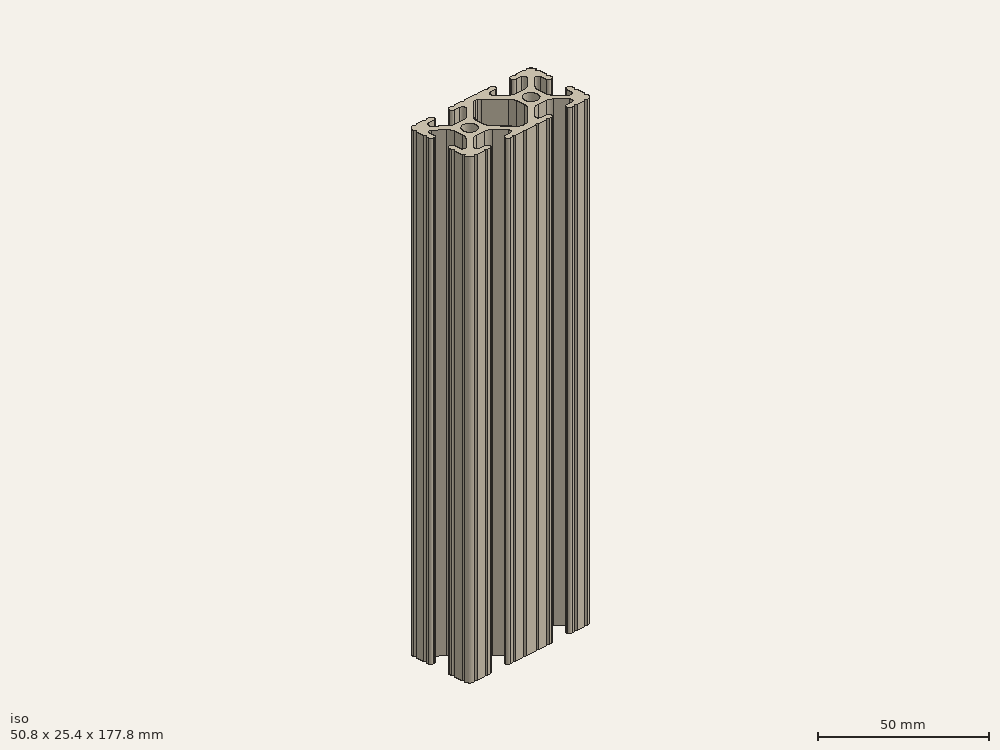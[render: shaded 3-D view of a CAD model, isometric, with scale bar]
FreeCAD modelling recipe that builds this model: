
FCSTD DOCUMENT  (FreeCAD 0.19R24267 (Git))
Label: 1020-7
License: All rights reserved
LicenseURL: http://en.wikipedia.org/wiki/All_rights_reserved
objects: Sketcher::SketchObject×1, Part::Extrusion×1
note: 2 computed .brp shape members not serialized (recipe doc carries the construction recipe); baked Part::Feature solids carry a one-line shape summary decoded from their .brp

FEATURE [Sketcher::SketchObject] Sketch162
  FullyConstrained = false
  sketch-geometry (162):
    g0: LineSegment StartX=7.25951 StartY=3.86941 StartZ=0 EndX=1.54575 EndY=9.57277 EndZ=0
    g1: LineSegment StartX=8.41248 StartY=-10.4902 StartZ=0 EndX=6.28364 EndY=-10.4902 EndZ=0
    g2: ArcOfCircle CenterX=8.41255 CenterY=-11.651 CenterZ=0 NormalX=0 NormalY=0 NormalZ=1 AngleXU=0 Radius=1.04895 StartAngle=4.71239 EndAngle=6.28319
    g3: LineSegment StartX=5.53258 StartY=-8.66607 StartZ=0 EndX=8.80999 EndY=-5.41626 EndZ=0
    g4: LineSegment StartX=9.4615 StartY=-11.651 StartZ=0 EndX=9.4615 EndY=-11.5392 EndZ=0
    g5: ArcOfCircle CenterX=8.41248 CenterY=-11.5392 CenterZ=0 NormalX=0 NormalY=0 NormalZ=1 AngleXU=0 Radius=1.04902 StartAngle=1.15714e-07 EndAngle=1.5708
    g6: ArcOfCircle CenterX=6.28364 CenterY=-9.42351 CenterZ=0 NormalX=0 NormalY=0 NormalZ=1 AngleXU=0 Radius=1.06669 StartAngle=2.35197 EndAngle=4.71239
    g7: LineSegment StartX=-7.28286 StartY=-3.84586 StartZ=0 EndX=-1.67557 EndY=-9.56109 EndZ=0
    g8: LineSegment StartX=1.50403 StartY=-9.57645 StartZ=0 EndX=7.25205 EndY=-3.87684 EndZ=0
    g9: LineSegment StartX=-0.551457 StartY=-10.033 StartZ=0 EndX=0.3952 EndY=-10.033 EndZ=0
    g10: LineSegment StartX=-1.54575 StartY=9.57277 StartZ=0 EndX=-7.25951 EndY=3.86941 EndZ=0
    g11: ArcOfCircle CenterX=0.3952 CenterY=-8.4582 CenterZ=0 NormalX=0 NormalY=0 NormalZ=1 AngleXU=0 Radius=1.5748 StartAngle=4.71239 EndAngle=5.49356
    g12: ArcOfCircle CenterX=5.0165 CenterY=-1.6223 CenterZ=0 NormalX=0 NormalY=0 NormalZ=1 AngleXU=0 Radius=3.175 StartAngle=5.49356 EndAngle=6.28319
    g13: LineSegment StartX=8.1915 StartY=-1.6223 StartZ=0 EndX=8.1915 EndY=1.6223 EndZ=0
    g14: LineSegment StartX=0.433213 StartY=10.033 StartZ=0 EndX=-0.433213 EndY=10.033 EndZ=0
    g15: ArcOfCircle CenterX=-0.551456 CenterY=-8.4582 CenterZ=0 NormalX=0 NormalY=0 NormalZ=1 AngleXU=0 Radius=1.5748 StartAngle=3.91746 EndAngle=4.71239
    g16: ArcOfCircle CenterX=-5.0165 CenterY=1.6223 CenterZ=0 NormalX=0 NormalY=0 NormalZ=1 AngleXU=0 Radius=3.175 StartAngle=2.35528 EndAngle=3.14159
    g17: ArcOfCircle CenterX=-0.433213 CenterY=8.4582 CenterZ=0 NormalX=0 NormalY=0 NormalZ=1 AngleXU=0 Radius=1.5748 StartAngle=1.5708 EndAngle=2.35528
    g18: ArcOfCircle CenterX=5.0165 CenterY=1.6223 CenterZ=0 NormalX=0 NormalY=0 NormalZ=1 AngleXU=0 Radius=3.175 StartAngle=2.15656e-07 EndAngle=0.78631
    g19: Circle CenterX=12.7 CenterY=-2.5e-15 CenterZ=0 NormalX=0 NormalY=0 NormalZ=-1 AngleXU=0 Radius=2.6035
    g20: Circle CenterX=-12.7 CenterY=2.5e-15 CenterZ=0 NormalX=0 NormalY=0 NormalZ=-1 AngleXU=0 Radius=2.6035
    g21: LineSegment StartX=-8.1915 StartY=1.6223 StartZ=0 EndX=-8.1915 EndY=-1.6223 EndZ=0
    g22: LineSegment StartX=-2.13358 StartY=-12.7 StartZ=0 EndX=2.13358 EndY=-12.7 EndZ=0
    g23: ArcOfCircle CenterX=-5.0165 CenterY=-1.6223 CenterZ=0 NormalX=0 NormalY=0 NormalZ=1 AngleXU=0 Radius=3.175 StartAngle=3.14159 EndAngle=3.91746
    g24: LineSegment StartX=3.14958 StartY=-12.7 StartZ=0 EndX=6.3669 EndY=-12.7 EndZ=0
    g25: ArcOfCircle CenterX=6.8749 CenterY=-12.7 CenterZ=0 NormalX=0 NormalY=0 NormalZ=1 AngleXU=0 Radius=0.508 StartAngle=0 EndAngle=3.14159
    g26: LineSegment StartX=-6.28939 StartY=-10.4902 StartZ=0 EndX=-8.41248 EndY=-10.4902 EndZ=0
    g27: LineSegment StartX=-8.41255 StartY=-12.7 StartZ=0 EndX=-7.38288 EndY=-12.7 EndZ=0
    g28: ArcOfCircle CenterX=0.433213 CenterY=8.4582 CenterZ=0 NormalX=0 NormalY=0 NormalZ=1 AngleXU=0 Radius=1.5748 StartAngle=0.78631 EndAngle=1.5708
    g29: ArcOfCircle CenterX=2.64158 CenterY=-12.7 CenterZ=0 NormalX=0 NormalY=0 NormalZ=1 AngleXU=0 Radius=0.508 StartAngle=0 EndAngle=3.14159
    g30: ArcOfCircle CenterX=-16.9875 CenterY=-11.5392 CenterZ=0 NormalX=0 NormalY=0 NormalZ=1 AngleXU=0 Radius=1.04902 StartAngle=1.16223e-07 EndAngle=1.5708
    g31: LineSegment StartX=-8.81696 StartY=-5.44724 StartZ=0 EndX=-5.56415 EndY=-8.76265 EndZ=0
    g32: LineSegment StartX=-16.9875 StartY=-10.4902 StartZ=0 EndX=-19.1164 EndY=-10.4902 EndZ=0
    g33: ArcOfCircle CenterX=-11.0833 CenterY=-7.6708 CenterZ=0 NormalX=0 NormalY=0 NormalZ=1 AngleXU=0 Radius=3.175 StartAngle=0.775866 EndAngle=1.5708
    g34: ArcOfCircle CenterX=-14.3449 CenterY=-7.6708 CenterZ=0 NormalX=0 NormalY=0 NormalZ=1 AngleXU=0 Radius=3.175 StartAngle=1.5708 EndAngle=2.3692
    g35: ArcOfCircle CenterX=-19.1164 CenterY=-9.4742 CenterZ=0 NormalX=0 NormalY=0 NormalZ=1 AngleXU=0 Radius=1.016 StartAngle=2.3692 EndAngle=4.71239
    g36: ArcOfCircle CenterX=-8.41248 CenterY=-11.5392 CenterZ=0 NormalX=0 NormalY=0 NormalZ=1 AngleXU=0 Radius=1.04902 StartAngle=1.5708 EndAngle=3.14159
    g37: LineSegment StartX=7.3829 StartY=-12.7 StartZ=0 EndX=8.41255 EndY=-12.7 EndZ=0
    g38: ArcOfCircle CenterX=-8.41255 CenterY=-11.651 CenterZ=0 NormalX=0 NormalY=0 NormalZ=1 AngleXU=0 Radius=1.04895 StartAngle=3.14159 EndAngle=4.71239
    g39: ArcOfCircle CenterX=14.3545 CenterY=-7.6708 CenterZ=0 NormalX=0 NormalY=0 NormalZ=1 AngleXU=0 Radius=3.175 StartAngle=0.789627 EndAngle=1.5708
    g40: ArcOfCircle CenterX=20.3835 CenterY=-1.55362 CenterZ=0 NormalX=0 NormalY=0 NormalZ=1 AngleXU=0 Radius=3.175 StartAngle=3.14159 EndAngle=3.93122
    g41: LineSegment StartX=23.1902 StartY=6.498 StartZ=0 EndX=23.1902 EndY=4.28752 EndZ=0
    g42: LineSegment StartX=-14.3449 StartY=-4.4958 StartZ=0 EndX=-11.0833 EndY=-4.4958 EndZ=0
    g43: LineSegment StartX=-19.8441 StartY=-8.76517 StartZ=0 EndX=-16.619 EndY=-5.45511 EndZ=0
    g44: LineSegment StartX=-6.36688 StartY=-12.7 StartZ=0 EndX=-3.14958 EndY=-12.7 EndZ=0
    g45: ArcOfCircle CenterX=-6.28939 CenterY=-9.4742 CenterZ=0 NormalX=0 NormalY=0 NormalZ=1 AngleXU=0 Radius=1.016 StartAngle=4.71239 EndAngle=7.05905
    g46: LineSegment StartX=-9.4615 StartY=-11.5392 StartZ=0 EndX=-9.4615 EndY=-11.6511 EndZ=0
    g47: ArcOfCircle CenterX=-6.87488 CenterY=-12.7 CenterZ=0 NormalX=0 NormalY=0 NormalZ=1 AngleXU=0 Radius=0.508 StartAngle=0 EndAngle=3.14159
    g48: LineSegment StartX=-15.9385 StartY=-11.651 StartZ=0 EndX=-15.9385 EndY=-11.5392 EndZ=0
    g49: ArcOfCircle CenterX=-2.64158 CenterY=-12.7 CenterZ=0 NormalX=0 NormalY=0 NormalZ=1 AngleXU=0 Radius=0.508 StartAngle=0 EndAngle=3.14159
    g50: ArcOfCircle CenterX=22.1596 CenterY=-6.33474 CenterZ=0 NormalX=0 NormalY=0 NormalZ=1 AngleXU=0 Radius=1.03057 StartAngle=3.93122 EndAngle=6.28319
    g51: ArcOfCircle CenterX=25.4 CenterY=5.82513 CenterZ=0 NormalX=0 NormalY=0 NormalZ=1 AngleXU=0 Radius=0.508 StartAngle=1.5708 EndAngle=4.71239
    g52: LineSegment StartX=25.4 StartY=6.33313 StartZ=0 EndX=25.4 EndY=9.5504 EndZ=0
    g53: LineSegment StartX=19.0331 StartY=-12.7 StartZ=0 EndX=22.2504 EndY=-12.7 EndZ=0
    g54: ArcOfCircle CenterX=20.3835 CenterY=1.69518 CenterZ=0 NormalX=0 NormalY=0 NormalZ=1 AngleXU=0 Radius=3.175 StartAngle=2.35528 EndAngle=3.14159
    g55: LineSegment StartX=16.9875 StartY=-12.7 StartZ=0 EndX=18.0171 EndY=-12.7 EndZ=0
    g56: ArcOfCircle CenterX=23.2918 CenterY=10.5918 CenterZ=0 NormalX=0 NormalY=0 NormalZ=1 AngleXU=0 Radius=2.1082 StartAngle=6.27114 EndAngle=7.86603
    g57: ArcOfCircle CenterX=24.2392 CenterY=-4.28752 CenterZ=0 NormalX=0 NormalY=0 NormalZ=1 AngleXU=0 Radius=1.04902 StartAngle=1.5708 EndAngle=3.14159
    g58: ArcOfCircle CenterX=24.401 CenterY=-4.23752 CenterZ=0 NormalX=0 NormalY=0 NormalZ=1 AngleXU=0 Radius=0.99902 StartAngle=1.41033e-07 EndAngle=1.5708
    g59: LineSegment StartX=16.59 StartY=-5.41626 StartZ=0 EndX=19.8674 EndY=-8.66607 EndZ=0
    g60: ArcOfCircle CenterX=16.9875 CenterY=-11.5392 CenterZ=0 NormalX=0 NormalY=0 NormalZ=1 AngleXU=0 Radius=1.04902 StartAngle=1.5708 EndAngle=3.14159
    g61: LineSegment StartX=22.2504 StartY=12.7 StartZ=0 EndX=19.0331 EndY=12.7 EndZ=0
    g62: ArcOfCircle CenterX=23.2918 CenterY=-10.5918 CenterZ=0 NormalX=0 NormalY=0 NormalZ=1 AngleXU=0 Radius=2.1082 StartAngle=4.70034 EndAngle=6.29523
    g63: ArcOfCircle CenterX=11.0455 CenterY=-7.6708 CenterZ=0 NormalX=0 NormalY=0 NormalZ=1 AngleXU=0 Radius=3.175 StartAngle=1.5708 EndAngle=2.35197
    g64: ArcOfCircle CenterX=22.7584 CenterY=12.7 CenterZ=0 NormalX=0 NormalY=0 NormalZ=1 AngleXU=0 Radius=0.508 StartAngle=3.14159 EndAngle=6.28288
    g65: LineSegment StartX=19.1164 StartY=-10.4902 StartZ=0 EndX=16.9875 EndY=-10.4902 EndZ=0
    g66: ArcOfCircle CenterX=22.7584 CenterY=-12.7 CenterZ=0 NormalX=0 NormalY=0 NormalZ=1 AngleXU=0 Radius=0.508 StartAngle=0.000301216 EndAngle=3.14159
    g67: ArcOfCircle CenterX=16.9875 CenterY=11.651 CenterZ=0 NormalX=0 NormalY=0 NormalZ=1 AngleXU=0 Radius=1.04902 StartAngle=1.5708 EndAngle=3.14159
    g68: ArcOfCircle CenterX=24.351 CenterY=4.28752 CenterZ=0 NormalX=0 NormalY=0 NormalZ=1 AngleXU=0 Radius=1.04902 StartAngle=4.71239 EndAngle=6.28319
    g69: ArcOfCircle CenterX=19.1164 CenterY=9.4742 CenterZ=0 NormalX=0 NormalY=0 NormalZ=1 AngleXU=0 Radius=1.016 StartAngle=5.49688 EndAngle=7.85398
    g70: LineSegment StartX=19.8341 StartY=8.75512 StartZ=0 EndX=16.4966 EndY=5.42369 EndZ=0
    g71: LineSegment StartX=18.0171 StartY=12.7 StartZ=0 EndX=16.9875 EndY=12.7 EndZ=0
    g72: ArcOfCircle CenterX=18.5251 CenterY=-12.7 CenterZ=0 NormalX=0 NormalY=0 NormalZ=1 AngleXU=0 Radius=0.508 StartAngle=0 EndAngle=3.14159
    g73: LineSegment StartX=15.9384 StartY=11.651 StartZ=0 EndX=15.9384 EndY=11.5392 EndZ=0
    g74: LineSegment StartX=16.9875 StartY=10.4902 StartZ=0 EndX=19.1164 EndY=10.4902 EndZ=0
    g75: LineSegment StartX=11.0455 StartY=-4.4958 StartZ=0 EndX=14.3545 EndY=-4.4958 EndZ=0
    g76: ArcOfCircle CenterX=14.2536 CenterY=7.6708 CenterZ=0 NormalX=0 NormalY=0 NormalZ=1 AngleXU=0 Radius=3.175 StartAngle=4.71239 EndAngle=5.49688
    g77: ArcOfCircle CenterX=25.4 CenterY=-5.82508 CenterZ=0 NormalX=0 NormalY=0 NormalZ=1 AngleXU=0 Radius=0.508 StartAngle=1.5708 EndAngle=4.71239
    g78: LineSegment StartX=18.1405 StartY=3.94229 StartZ=0 EndX=21.4316 EndY=7.22739 EndZ=0
    g79: LineSegment StartX=25.4 StartY=-5.31708 StartZ=0 EndX=25.4 EndY=-4.23752 EndZ=0
    g80: LineSegment StartX=14.2536 StartY=4.4958 StartZ=0 EndX=11.1464 EndY=4.4958 EndZ=0
    g81: ArcOfCircle CenterX=18.5251 CenterY=12.7 CenterZ=0 NormalX=0 NormalY=0 NormalZ=1 AngleXU=0 Radius=0.508 StartAngle=3.14159 EndAngle=6.28319
    g82: LineSegment StartX=23.1902 StartY=-4.28752 StartZ=0 EndX=23.1902 EndY=-6.33474 EndZ=0
    g83: LineSegment StartX=24.401 StartY=-3.2385 StartZ=0 EndX=24.2392 EndY=-3.2385 EndZ=0
    g84: ArcOfCircle CenterX=22.1596 CenterY=6.498 CenterZ=0 NormalX=0 NormalY=0 NormalZ=1 AngleXU=0 Radius=1.03057 StartAngle=0 EndAngle=2.35528
    g85: LineSegment StartX=15.9385 StartY=-11.5392 StartZ=0 EndX=15.9385 EndY=-11.6511 EndZ=0
    g86: LineSegment StartX=25.4 StartY=4.28752 StartZ=0 EndX=25.4 EndY=5.31713 EndZ=0
    g87: ArcOfCircle CenterX=11.1464 CenterY=7.6708 CenterZ=0 NormalX=0 NormalY=0 NormalZ=1 AngleXU=0 Radius=3.175 StartAngle=3.9279 EndAngle=4.71239
    g88: LineSegment StartX=8.90339 StartY=5.42369 StartZ=0 EndX=5.56588 EndY=8.75512 EndZ=0
    g89: LineSegment StartX=21.434 StartY=-7.06654 StartZ=0 EndX=18.148 EndY=-3.80816 EndZ=0
    g90: ArcOfCircle CenterX=25.4 CenterY=10.0584 CenterZ=0 NormalX=0 NormalY=0 NormalZ=1 AngleXU=0 Radius=0.508 StartAngle=1.5711 EndAngle=4.71239
    g91: ArcOfCircle CenterX=16.9875 CenterY=-11.651 CenterZ=0 NormalX=0 NormalY=0 NormalZ=1 AngleXU=0 Radius=1.04895 StartAngle=3.14159 EndAngle=4.71239
    g92: ArcOfCircle CenterX=19.1164 CenterY=-9.42352 CenterZ=0 NormalX=0 NormalY=0 NormalZ=1 AngleXU=0 Radius=1.06668 StartAngle=4.71239 EndAngle=7.07281
    g93: ArcOfCircle CenterX=24.2392 CenterY=4.28752 CenterZ=0 NormalX=0 NormalY=0 NormalZ=1 AngleXU=0 Radius=1.04902 StartAngle=3.14159 EndAngle=4.71239
    g94: ArcOfCircle CenterX=16.9875 CenterY=11.5392 CenterZ=0 NormalX=0 NormalY=0 NormalZ=1 AngleXU=0 Radius=1.04902 StartAngle=3.14159 EndAngle=4.71239
    g95: ArcOfCircle CenterX=25.4 CenterY=-10.0584 CenterZ=0 NormalX=0 NormalY=0 NormalZ=1 AngleXU=0 Radius=0.508 StartAngle=1.5708 EndAngle=4.71209
    g96: ArcOfCircle CenterX=6.87487 CenterY=12.7 CenterZ=0 NormalX=0 NormalY=0 NormalZ=1 AngleXU=0 Radius=0.508 StartAngle=3.14159 EndAngle=6.28319
    g97: LineSegment StartX=25.4 StartY=-9.5504 StartZ=0 EndX=25.4 EndY=-6.33308 EndZ=0
    g98: LineSegment StartX=17.2085 StartY=-1.55362 StartZ=0 EndX=17.2085 EndY=1.69518 EndZ=0
    g99: LineSegment StartX=-9.46155 StartY=11.651 StartZ=0 EndX=-9.46155 EndY=11.5392 EndZ=0
    g100: LineSegment StartX=24.2392 StartY=3.2385 StartZ=0 EndX=24.351 EndY=3.2385 EndZ=0
    g101: LineSegment StartX=-8.41253 StartY=10.4902 StartZ=0 EndX=-6.28939 EndY=10.4902 EndZ=0
    g102: ArcOfCircle CenterX=-10.8409 CenterY=7.6708 CenterZ=0 NormalX=0 NormalY=0 NormalZ=1 AngleXU=0 Radius=3.175 StartAngle=4.71239 EndAngle=5.49688
    g103: LineSegment StartX=-19.1164 StartY=10.4902 StartZ=0 EndX=-16.9875 EndY=10.4902 EndZ=0
    g104: LineSegment StartX=-10.8409 StartY=4.4958 StartZ=0 EndX=-14.1026 EndY=4.4958 EndZ=0
    g105: LineSegment StartX=-16.1879 StartY=5.27664 StartZ=0 EndX=-19.8682 EndY=8.48225 EndZ=0
    g106: LineSegment StartX=-7.38291 StartY=12.7 StartZ=0 EndX=-8.41253 EndY=12.7 EndZ=0
    g107: ArcOfCircle CenterX=-6.28939 CenterY=9.34546 CenterZ=0 NormalX=0 NormalY=0 NormalZ=1 AngleXU=0 Radius=1.14474 StartAngle=5.49688 EndAngle=7.85398
    g108: LineSegment StartX=6.28364 StartY=10.4902 StartZ=0 EndX=8.41253 EndY=10.4902 EndZ=0
    g109: ArcOfCircle CenterX=8.41253 CenterY=11.651 CenterZ=0 NormalX=0 NormalY=0 NormalZ=1 AngleXU=0 Radius=1.04902 StartAngle=4.29175e-07 EndAngle=1.5708
    g110: LineSegment StartX=9.46155 StartY=11.5392 StartZ=0 EndX=9.46155 EndY=11.651 EndZ=0
    g111: ArcOfCircle CenterX=-14.1026 CenterY=7.6708 CenterZ=0 NormalX=0 NormalY=0 NormalZ=1 AngleXU=0 Radius=3.175 StartAngle=3.99583 EndAngle=4.71239
    g112: LineSegment StartX=-5.48068 StartY=8.53527 StartZ=0 EndX=-8.59793 EndY=5.42369 EndZ=0
    g113: ArcOfCircle CenterX=-19.1164 CenterY=9.34546 CenterZ=0 NormalX=0 NormalY=0 NormalZ=1 AngleXU=0 Radius=1.14474 StartAngle=1.5708 EndAngle=3.99583
    g114: LineSegment StartX=8.41253 StartY=12.7 StartZ=0 EndX=7.38287 EndY=12.7 EndZ=0
    g115: LineSegment StartX=-3.14958 StartY=12.7 StartZ=0 EndX=-6.36691 EndY=12.7 EndZ=0
    g116: ArcOfCircle CenterX=-8.41253 CenterY=11.5392 CenterZ=0 NormalX=0 NormalY=0 NormalZ=1 AngleXU=0 Radius=1.04902 StartAngle=3.14159 EndAngle=4.71239
    g117: ArcOfCircle CenterX=8.41253 CenterY=11.5392 CenterZ=0 NormalX=0 NormalY=0 NormalZ=1 AngleXU=0 Radius=1.04902 StartAngle=4.71239 EndAngle=6.28319
    g118: ArcOfCircle CenterX=-6.87491 CenterY=12.7 CenterZ=0 NormalX=0 NormalY=0 NormalZ=1 AngleXU=0 Radius=0.508 StartAngle=3.14159 EndAngle=6.28319
    g119: ArcOfCircle CenterX=-8.41253 CenterY=11.651 CenterZ=0 NormalX=0 NormalY=0 NormalZ=1 AngleXU=0 Radius=1.04902 StartAngle=1.5708 EndAngle=3.14159
    g120: ArcOfCircle CenterX=-2.64159 CenterY=12.7 CenterZ=0 NormalX=0 NormalY=0 NormalZ=1 AngleXU=0 Radius=0.507987 StartAngle=3.14159 EndAngle=6.28319
    g121: ArcOfCircle CenterX=6.28364 CenterY=9.4742 CenterZ=0 NormalX=0 NormalY=0 NormalZ=1 AngleXU=0 Radius=1.016 StartAngle=1.5708 EndAngle=3.9279
    g122: LineSegment StartX=2.13361 StartY=12.7 StartZ=0 EndX=-2.13361 EndY=12.7 EndZ=0
    g123: LineSegment StartX=6.36687 StartY=12.7 StartZ=0 EndX=3.14961 EndY=12.7 EndZ=0
    g124: ArcOfCircle CenterX=-24.401 CenterY=4.23752 CenterZ=0 NormalX=0 NormalY=0 NormalZ=1 AngleXU=0 Radius=0.99902 StartAngle=3.14159 EndAngle=4.71239
    g125: LineSegment StartX=-16.9875 StartY=12.7 StartZ=0 EndX=-18.0171 EndY=12.7 EndZ=0
    g126: LineSegment StartX=-24.401 StartY=3.2385 StartZ=0 EndX=-24.1892 EndY=3.2385 EndZ=0
    g127: ArcOfCircle CenterX=2.64161 CenterY=12.7 CenterZ=0 NormalX=0 NormalY=0 NormalZ=1 AngleXU=0 Radius=0.508 StartAngle=3.14159 EndAngle=6.28319
    g128: ArcOfCircle CenterX=-22.2207 CenterY=-6.67687 CenterZ=0 NormalX=0 NormalY=0 NormalZ=1 AngleXU=0 Radius=0.969476 StartAngle=3.14159 EndAngle=5.51079
    g129: LineSegment StartX=-18.1094 StartY=-3.8465 StartZ=0 EndX=-21.5263 EndY=-7.35342 EndZ=0
    g130: LineSegment StartX=-17.2085 StartY=1.63081 StartZ=0 EndX=-17.2085 EndY=-1.63081 EndZ=0
    g131: ArcOfCircle CenterX=-22.2207 CenterY=6.15588 CenterZ=0 NormalX=0 NormalY=0 NormalZ=1 AngleXU=0 Radius=0.969476 StartAngle=0.854233 EndAngle=3.14159
    g132: LineSegment StartX=-24.1892 StartY=-3.2385 StartZ=0 EndX=-24.401 EndY=-3.2385 EndZ=0
    g133: ArcOfCircle CenterX=-25.4 CenterY=10.0584 CenterZ=0 NormalX=0 NormalY=0 NormalZ=1 AngleXU=0 Radius=0.508 StartAngle=4.71239 EndAngle=7.85368
    g134: LineSegment StartX=-23.1902 StartY=-6.67687 StartZ=0 EndX=-23.1902 EndY=-4.23752 EndZ=0
    g135: ArcOfCircle CenterX=-20.3835 CenterY=-1.63081 CenterZ=0 NormalX=0 NormalY=0 NormalZ=1 AngleXU=0 Radius=3.175 StartAngle=5.51079 EndAngle=6.28319
    g136: ArcOfCircle CenterX=-24.1892 CenterY=-4.23752 CenterZ=0 NormalX=0 NormalY=0 NormalZ=1 AngleXU=0 Radius=0.99902 StartAngle=1.41033e-07 EndAngle=1.5708
    g137: ArcOfCircle CenterX=-25.4 CenterY=5.82508 CenterZ=0 NormalX=0 NormalY=0 NormalZ=1 AngleXU=0 Radius=0.508 StartAngle=4.71239 EndAngle=7.85398
    g138: LineSegment StartX=-23.1902 StartY=4.23752 StartZ=0 EndX=-23.1902 EndY=6.15588 EndZ=0
    g139: LineSegment StartX=-15.9384 StartY=11.5392 StartZ=0 EndX=-15.9384 EndY=11.651 EndZ=0
    g140: ArcOfCircle CenterX=-22.7584 CenterY=12.7 CenterZ=0 NormalX=0 NormalY=0 NormalZ=1 AngleXU=0 Radius=0.508 StartAngle=3.14189 EndAngle=6.28319
    g141: LineSegment StartX=-19.0331 StartY=12.7 StartZ=0 EndX=-22.2504 EndY=12.7 EndZ=0
    g142: ArcOfCircle CenterX=-16.9875 CenterY=11.651 CenterZ=0 NormalX=0 NormalY=0 NormalZ=1 AngleXU=0 Radius=1.04902 StartAngle=4.28571e-07 EndAngle=1.5708
    g143: ArcOfCircle CenterX=-18.5251 CenterY=12.7 CenterZ=0 NormalX=0 NormalY=0 NormalZ=1 AngleXU=0 Radius=0.508 StartAngle=3.14159 EndAngle=6.28319
    g144: ArcOfCircle CenterX=-24.1892 CenterY=4.23752 CenterZ=0 NormalX=0 NormalY=0 NormalZ=1 AngleXU=0 Radius=0.99902 StartAngle=4.71239 EndAngle=6.28319
    g145: LineSegment StartX=-25.4 StartY=5.31708 StartZ=0 EndX=-25.4 EndY=4.23752 EndZ=0
    g146: ArcOfCircle CenterX=-16.9875 CenterY=11.5392 CenterZ=0 NormalX=0 NormalY=0 NormalZ=1 AngleXU=0 Radius=1.04902 StartAngle=4.71239 EndAngle=6.28319
    g147: LineSegment StartX=-21.584 StartY=6.88693 StartZ=0 EndX=-18.2982 EndY=4.02497 EndZ=0
    g148: ArcOfCircle CenterX=-20.3835 CenterY=1.63081 CenterZ=0 NormalX=0 NormalY=0 NormalZ=1 AngleXU=0 Radius=3.175 StartAngle=0 EndAngle=0.854233
    g149: ArcOfCircle CenterX=-23.2918 CenterY=10.5918 CenterZ=0 NormalX=0 NormalY=0 NormalZ=1 AngleXU=0 Radius=2.1082 StartAngle=1.55875 EndAngle=3.15364
    g150: LineSegment StartX=-25.4 StartY=9.5504 StartZ=0 EndX=-25.4 EndY=6.33308 EndZ=0
    g151: LineSegment StartX=-25.4 StartY=-4.23752 StartZ=0 EndX=-25.4 EndY=-5.31708 EndZ=0
    g152: ArcOfCircle CenterX=-23.2918 CenterY=-10.5918 CenterZ=0 NormalX=0 NormalY=0 NormalZ=1 AngleXU=0 Radius=2.1082 StartAngle=3.12954 EndAngle=4.72444
    g153: ArcOfCircle CenterX=-22.7584 CenterY=-12.7 CenterZ=0 NormalX=0 NormalY=0 NormalZ=1 AngleXU=0 Radius=0.508 StartAngle=0 EndAngle=3.14129
    g154: LineSegment StartX=-18.0171 StartY=-12.7 StartZ=0 EndX=-16.9875 EndY=-12.7 EndZ=0
    g155: ArcOfCircle CenterX=-25.4 CenterY=-10.0584 CenterZ=0 NormalX=0 NormalY=0 NormalZ=1 AngleXU=0 Radius=0.508 StartAngle=4.71269 EndAngle=7.85398
    g156: LineSegment StartX=-22.2504 StartY=-12.7 StartZ=0 EndX=-19.0331 EndY=-12.7 EndZ=0
    g157: ArcOfCircle CenterX=-16.9875 CenterY=-11.651 CenterZ=0 NormalX=0 NormalY=0 NormalZ=1 AngleXU=0 Radius=1.04895 StartAngle=4.71239 EndAngle=6.28319
    g158: ArcOfCircle CenterX=-24.401 CenterY=-4.23752 CenterZ=0 NormalX=0 NormalY=0 NormalZ=1 AngleXU=0 Radius=0.99902 StartAngle=1.5708 EndAngle=3.14159
    g159: ArcOfCircle CenterX=-25.4 CenterY=-5.82513 CenterZ=0 NormalX=0 NormalY=0 NormalZ=1 AngleXU=0 Radius=0.508051 StartAngle=4.71239 EndAngle=7.85398
    g160: ArcOfCircle CenterX=-18.5251 CenterY=-12.7 CenterZ=0 NormalX=0 NormalY=0 NormalZ=1 AngleXU=0 Radius=0.508 StartAngle=0 EndAngle=3.14159
    g161: LineSegment StartX=-25.4 StartY=-6.33319 StartZ=0 EndX=-25.4 EndY=-9.5504 EndZ=0
  constraints (160):
    c: Coincident(g161,g155)
    c: Coincident(g159,g161)
    c: Coincident(g151,g159)
    c: Coincident(g158,g151)
    c: Coincident(g124,g145)
    c: Coincident(g137,g145)
    c: Coincident(g137,g150)
    c: Coincident(g133,g150)
    c: Coincident(g152,g155)
    c: Coincident(g149,g133)
    c: Coincident(g158,g132)
    c: Coincident(g124,g126)
    c: Coincident(g136,g132)
    c: Coincident(g144,g126)
    c: Coincident(g153,g152)
    c: Coincident(g140,g149)
    c: Coincident(g134,g128)
    c: Coincident(g134,g136)
    c: Coincident(g138,g144)
    c: Coincident(g131,g138)
    c: Coincident(g153,g156)
    c: Coincident(g141,g140)
    c: Coincident(g131,g147)
    c: Coincident(g129,g128)
    c: Coincident(g105,g113)
    c: Coincident(g35,g43)
    c: Coincident(g35,g32)
    c: Coincident(g113,g103)
    c: Coincident(g156,g160)
    c: Coincident(g143,g141)
    c: Coincident(g147,g148)
    c: Coincident(g135,g129)
    c: Coincident(g154,g160)
    c: Coincident(g143,g125)
    c: Coincident(g130,g135)
    c: Coincident(g130,g148)
    c: Coincident(g154,g157)
    c: Coincident(g32,g30)
    c: Coincident(g103,g146)
    c: Coincident(g142,g125)
    c: Coincident(g43,g34)
    c: Coincident(g111,g105)
    c: Coincident(g157,g48)
    c: Coincident(g48,g30)
    c: Coincident(g139,g146)
    c: Coincident(g139,g142)
    c: Coincident(g42,g34)
    c: Coincident(g104,g111)
    c: Coincident(g33,g42)
    c: Coincident(g102,g104)
    c: Coincident(g38,g46)
    c: Coincident(g46,g36)
    c: Coincident(g99,g116)
    c: Coincident(g119,g99)
    c: Coincident(g33,g31)
    c: Coincident(g102,g112)
    c: Coincident(g27,g38)
    c: Coincident(g36,g26)
    c: Coincident(g116,g101)
    c: Coincident(g106,g119)
    c: Coincident(g21,g23)
    c: Coincident(g21,g16)
    c: Coincident(g27,g47)
    c: Coincident(g106,g118)
    c: Coincident(g23,g7)
    c: Coincident(g10,g16)
    c: Coincident(g44,g47)
    c: Coincident(g118,g115)
    c: Coincident(g45,g26)
    c: Coincident(g107,g101)
    c: Coincident(g45,g31)
    c: Coincident(g112,g107)
    c: Coincident(g44,g49)
    c: Coincident(g120,g115)
    c: Coincident(g22,g49)
    c: Coincident(g122,g120)
    c: Coincident(g15,g7)
    c: Coincident(g10,g17)
    c: Coincident(g9,g15)
    c: Coincident(g17,g14)
    c: Coincident(g9,g11)
    c: Coincident(g14,g28)
    c: Coincident(g8,g11)
    c: Coincident(g0,g28)
    c: Coincident(g29,g22)
    c: Coincident(g122,g127)
    c: Coincident(g24,g29)
    c: Coincident(g123,g127)
    c: Coincident(g3,g6)
    c: Coincident(g88,g121)
    c: Coincident(g1,g6)
    c: Coincident(g108,g121)
    c: Coincident(g25,g24)
    c: Coincident(g96,g123)
    c: Coincident(g8,g12)
    c: Coincident(g18,g0)
    c: Coincident(g25,g37)
    c: Coincident(g96,g114)
    c: Coincident(g12,g13)
    c: Coincident(g18,g13)
    c: Coincident(g2,g37)
    c: Coincident(g5,g1)
    c: Coincident(g117,g108)
    c: Coincident(g109,g114)
    c: Coincident(g3,g63)
    c: Coincident(g87,g88)
    c: Coincident(g2,g4)
    c: Coincident(g5,g4)
    c: Coincident(g117,g110)
    c: Coincident(g109,g110)
    c: Coincident(g75,g63)
    c: Coincident(g80,g87)
    c: Coincident(g80,g76)
    c: Coincident(g39,g75)
    c: Coincident(g85,g91)
    c: Coincident(g85,g60)
    c: Coincident(g73,g94)
    c: Coincident(g73,g67)
    c: Coincident(g70,g76)
    c: Coincident(g59,g39)
    c: Coincident(g55,g91)
    c: Coincident(g60,g65)
    c: Coincident(g94,g74)
    c: Coincident(g67,g71)
    c: Coincident(g40,g98)
    c: Coincident(g54,g98)
    c: Coincident(g55,g72)
    c: Coincident(g71,g81)
    c: Coincident(g78,g54)
    c: Coincident(g40,g89)
    c: Coincident(g53,g72)
    c: Coincident(g61,g81)
    c: Coincident(g65,g92)
    c: Coincident(g74,g69)
    c: Coincident(g70,g69)
    c: Coincident(g59,g92)
    c: Coincident(g84,g78)
    c: Coincident(g50,g89)
    c: Coincident(g53,g66)
    c: Coincident(g64,g61)
    c: Coincident(g82,g50)
    c: Coincident(g57,g82)
    c: Coincident(g41,g93)
    c: Coincident(g41,g84)
    c: Coincident(g62,g66)
    c: Coincident(g64,g56)
    c: Coincident(g57,g83)
    c: Coincident(g100,g93)
    c: Coincident(g100,g68)
    c: Coincident(g58,g83)
    c: Coincident(g62,g95)
    c: Coincident(g56,g90)
    c: Coincident(g97,g95)
    c: Coincident(g97,g77)
    c: Coincident(g77,g79)
    c: Coincident(g58,g79)
    c: Coincident(g68,g86)
    c: Coincident(g86,g51)
    c: Coincident(g51,g52)
    c: Coincident(g52,g90)
FEATURE [Part::Extrusion] Extrude
  Base = -> Sketch162
  Dir = (0,0,1)
  DirMode = 2
  FaceMakerClass = Part::FaceMakerBullseye
  LengthFwd = 177.8
  LengthRev = 0
  Solid = true
  Symmetric = false
